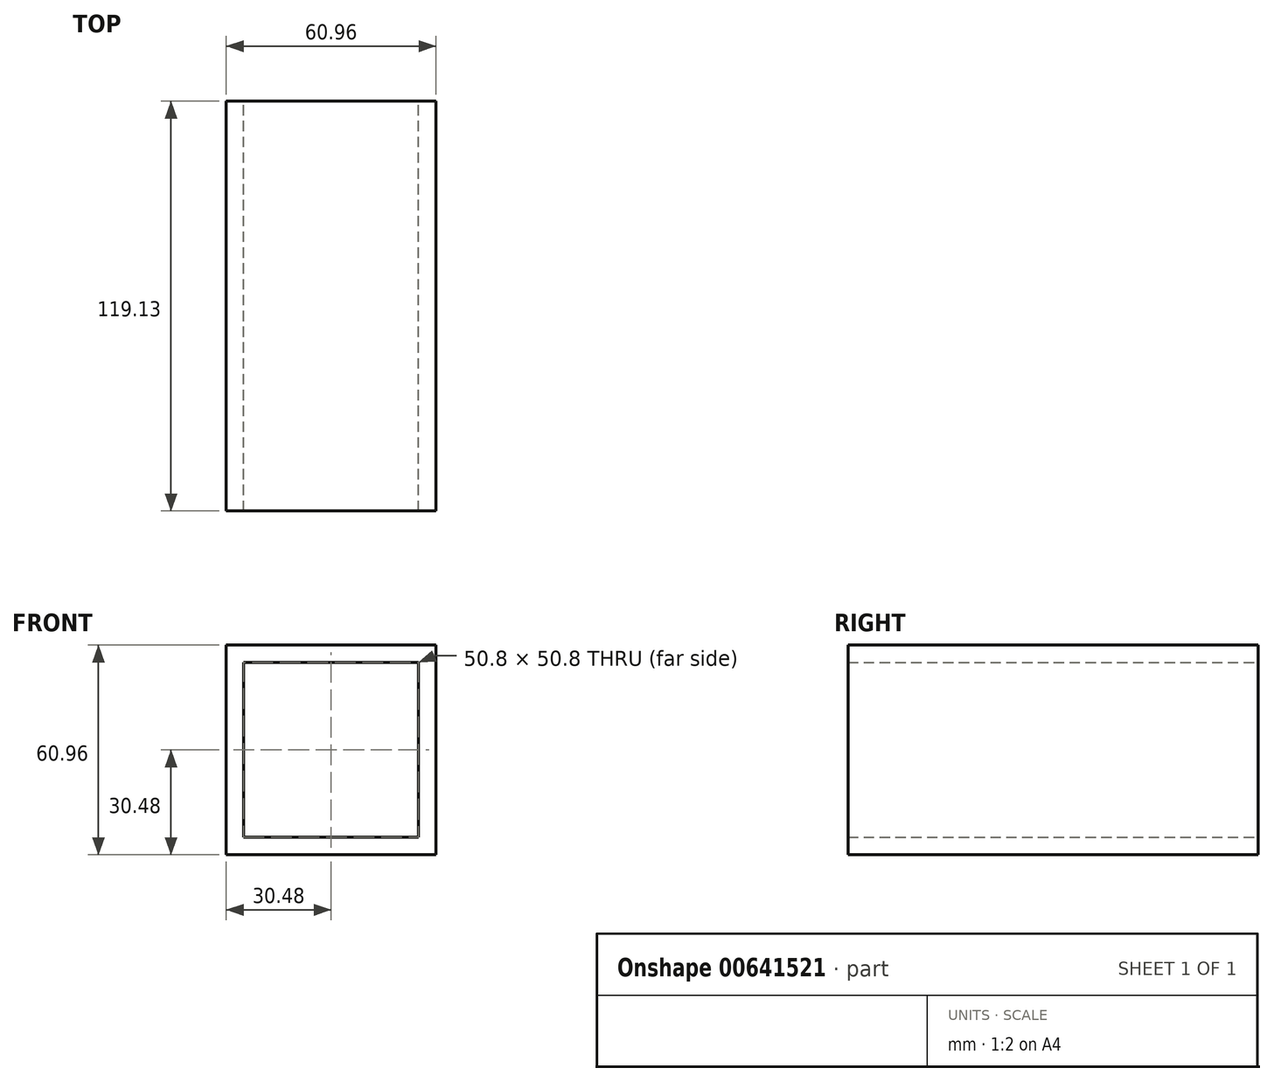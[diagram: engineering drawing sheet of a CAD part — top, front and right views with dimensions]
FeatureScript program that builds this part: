
annotation { "Feature Type Name" : "Feature", "Feature Type Description" : "" }
export const myFeature = defineFeature(function(context is Context, id is Id, definition is map)
    precondition{}
    {
        {
            var Q0;
            Q0=qCreatedBy(makeId("Front.planeOp"),FACE);
            var sketch = newSketch(context, id + "F0", { "sketchPlane" : qUnion([Q0])});
            skLineSegment(sketch, "E0.bottom", {"start": v(0, 0) * mm, "end": v(50.8, 0) * mm});
            skLineSegment(sketch, "E0.top", {"start": v(0, 50.8) * mm, "end": v(50.8, 50.8) * mm});
            skLineSegment(sketch, "E0.left", {"start": v(0, 0) * mm, "end": v(0, 50.8) * mm});
            skLineSegment(sketch, "E0.right", {"start": v(50.8, 0) * mm, "end": v(50.8, 50.8) * mm});
            skLineSegment(sketch, "E1.0", {"start": v(0, 55.88) * mm, "end": v(50.8, 55.88) * mm});
            skLineSegment(sketch, "E2.0", {"start": v(55.88, 0) * mm, "end": v(55.88, 50.8) * mm});
            skLineSegment(sketch, "E3.0", {"start": v(0, -5.08) * mm, "end": v(50.8, -5.08) * mm});
            skLineSegment(sketch, "E4.0", {"start": v(-5.08, 0) * mm, "end": v(-5.08, 50.8) * mm});
            skLineSegment(sketch, "E5", {"start": v(-5.08, 50.8) * mm, "end": v(-5.08, 55.88) * mm});
            skLineSegment(sketch, "E6", {"start": v(-5.08, 55.88) * mm, "end": v(0, 55.88) * mm});
            skLineSegment(sketch, "E7", {"start": v(50.8, 55.88) * mm, "end": v(55.88, 55.88) * mm});
            skLineSegment(sketch, "E8", {"start": v(55.88, 55.88) * mm, "end": v(55.88, 50.8) * mm});
            skLineSegment(sketch, "E9", {"start": v(55.88, 0) * mm, "end": v(55.88, -5.08) * mm});
            skLineSegment(sketch, "E10", {"start": v(55.88, -5.08) * mm, "end": v(50.8, -5.08) * mm});
            skLineSegment(sketch, "E11", {"start": v(0, -5.08) * mm, "end": v(-5.08, -5.08) * mm});
            skLineSegment(sketch, "E12", {"start": v(-5.08, -5.08) * mm, "end": v(-5.08, 0) * mm});
            skSolve(sketch);
        }
        {
            var Q0;
            Q0=makeQuery(id+"F0.imprint","IMPRINT",FACE,{"disambiguationData":[TD([[makeQuery(id+"F0.imprint","IMPRINT",EDGE,{"derivedFrom":sQuery(id+"F0.wireOp",EDGE,"E0.bottom")}),-1.0]])]});
            extrude(context, id + "F1", {"entities" : qUnion([Q0]), "depth" : 119.13 * mm, "offsetDistance" : 25.4 * mm});
        }
    });
